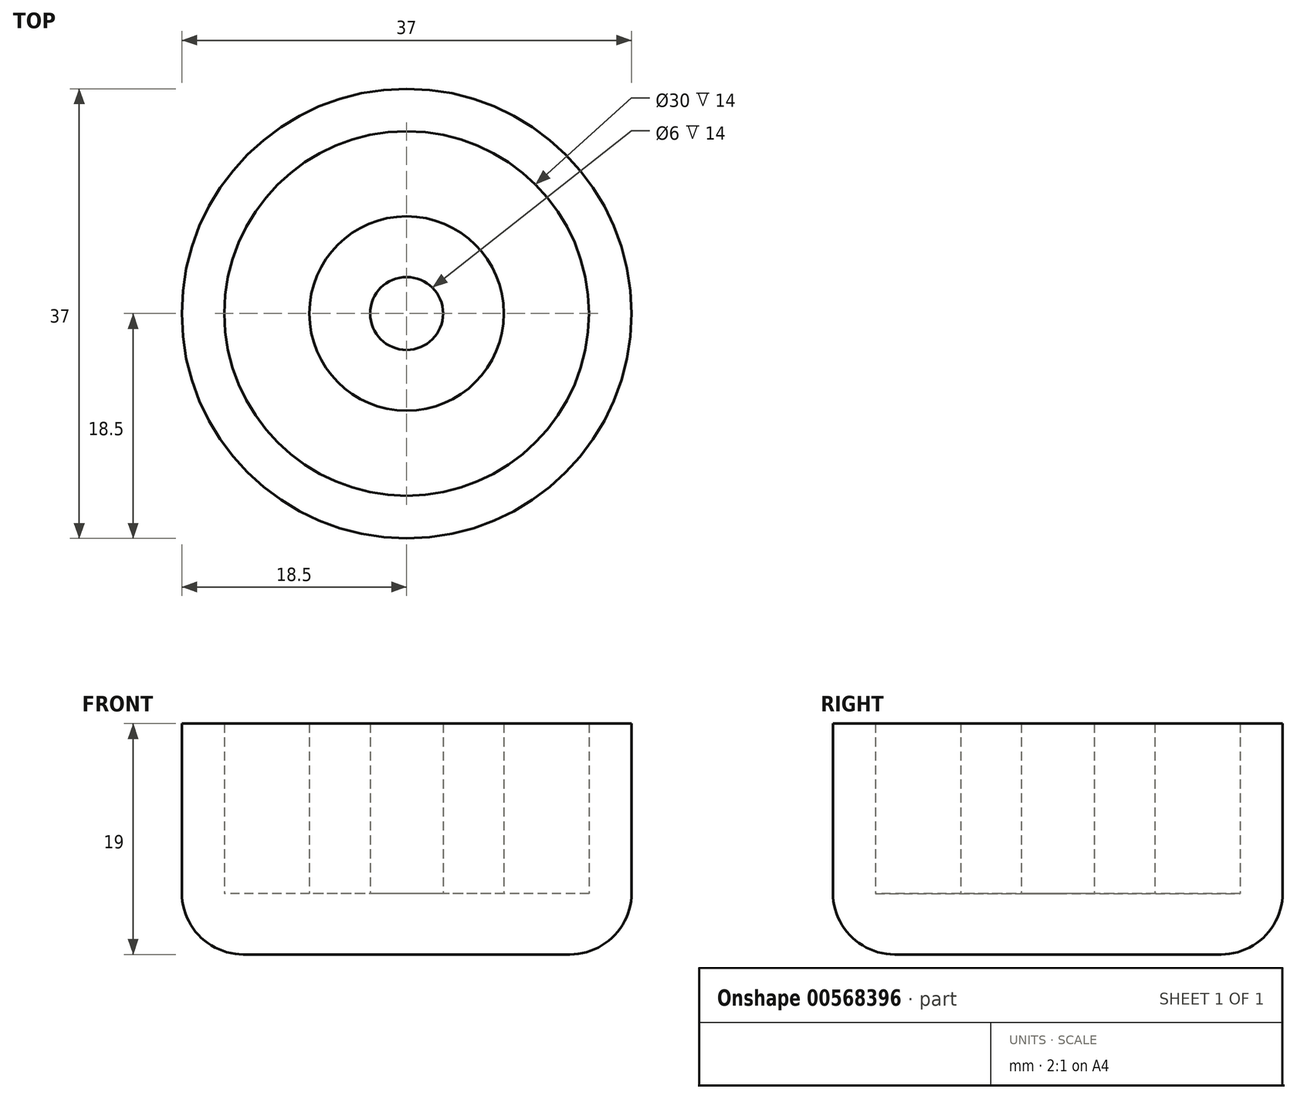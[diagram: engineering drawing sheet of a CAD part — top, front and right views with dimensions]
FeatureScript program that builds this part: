
annotation { "Feature Type Name" : "Feature", "Feature Type Description" : "" }
export const myFeature = defineFeature(function(context is Context, id is Id, definition is map)
    precondition{}
    {
        {
            var Q0;
            Q0=qCreatedBy(makeId("Top.planeOp"),FACE);
            var sketch = newSketch(context, id + "F0", { "sketchPlane" : qUnion([Q0])});
            skCircle(sketch, "E0", {"center": v(0, 0) * mm, "radius": 18.5 * mm});
            skSolve(sketch);
        }
        {
            var Q0;
            Q0 = qSketchRegion(id + "F0", true);
            extrude(context, id + "F1", {"entities" : qUnion([Q0]), "depth" : 5 * mm, "offsetDistance" : 25 * mm});
        }
        {
            var Q0;
            Q0=makeQuery(id+"F1.opExtrude","CAP_FACE",FACE,{"disambiguationData":[OSD([sQuery(id+"F0.wireOp",EDGE,"E0")])],"isStart":false});
            var sketch = newSketch(context, id + "F2", { "sketchPlane" : qUnion([Q0])});
            skCircle(sketch, "E1", {"center": v(0, 0) * mm, "radius": 15 * mm});
            skSolve(sketch);
        }
        {
            var Q0;
            Q0=makeQuery(id+"F2.imprint","IMPRINT",FACE,{"disambiguationData":[TD([[makeQuery(id+"F2.imprint","IMPRINT",EDGE,{"derivedFrom":sQuery(id+"F2.wireOp",EDGE,"E1")}),-1.0]])]});
            extrude(context, id + "F3", {"entities" : qUnion([Q0]), "operationType" : NewBodyOperationType.ADD, "depth" : 14 * mm, "offsetDistance" : 25 * mm});
        }
        {
            var Q0;
            Q0=makeQuery(id+"F1.opExtrude","CAP_FACE",FACE,{"disambiguationData":[OSD([sQuery(id+"F0.wireOp",EDGE,"E0")])],"isStart":true});
            fillet(context, id + "F4", {"entities" : qUnion([Q0]), "radius" : 5.07 * mm, "tangentPropagation" : true, "allowEdgeOverflow" : false});
        }
        {
            var Q0;
            Q0=makeQuery(id+"F1.opExtrude","CAP_FACE",FACE,{"disambiguationData":[OSD([sQuery(id+"F0.wireOp",EDGE,"E0")])],"isStart":false});
            var sketch = newSketch(context, id + "F5", { "sketchPlane" : qUnion([Q0])});
            skCircle(sketch, "E2", {"center": v(0, 0) * mm, "radius": 3 * mm});
            skCircle(sketch, "E3.0", {"center": v(0, 0) * mm, "radius": 8 * mm});
            skSolve(sketch);
        }
        {
            var Q0;
            Q0=makeQuery(id+"F5.imprint","IMPRINT",FACE,{"disambiguationData":[TD([[makeQuery(id+"F5.imprint","IMPRINT",EDGE,{"derivedFrom":sQuery(id+"F5.wireOp",EDGE,"E2")}),-1.0]])]});
            extrude(context, id + "F6", {"entities" : qUnion([Q0]), "operationType" : NewBodyOperationType.ADD, "depth" : 14 * mm, "offsetDistance" : 25 * mm});
        }
    });
